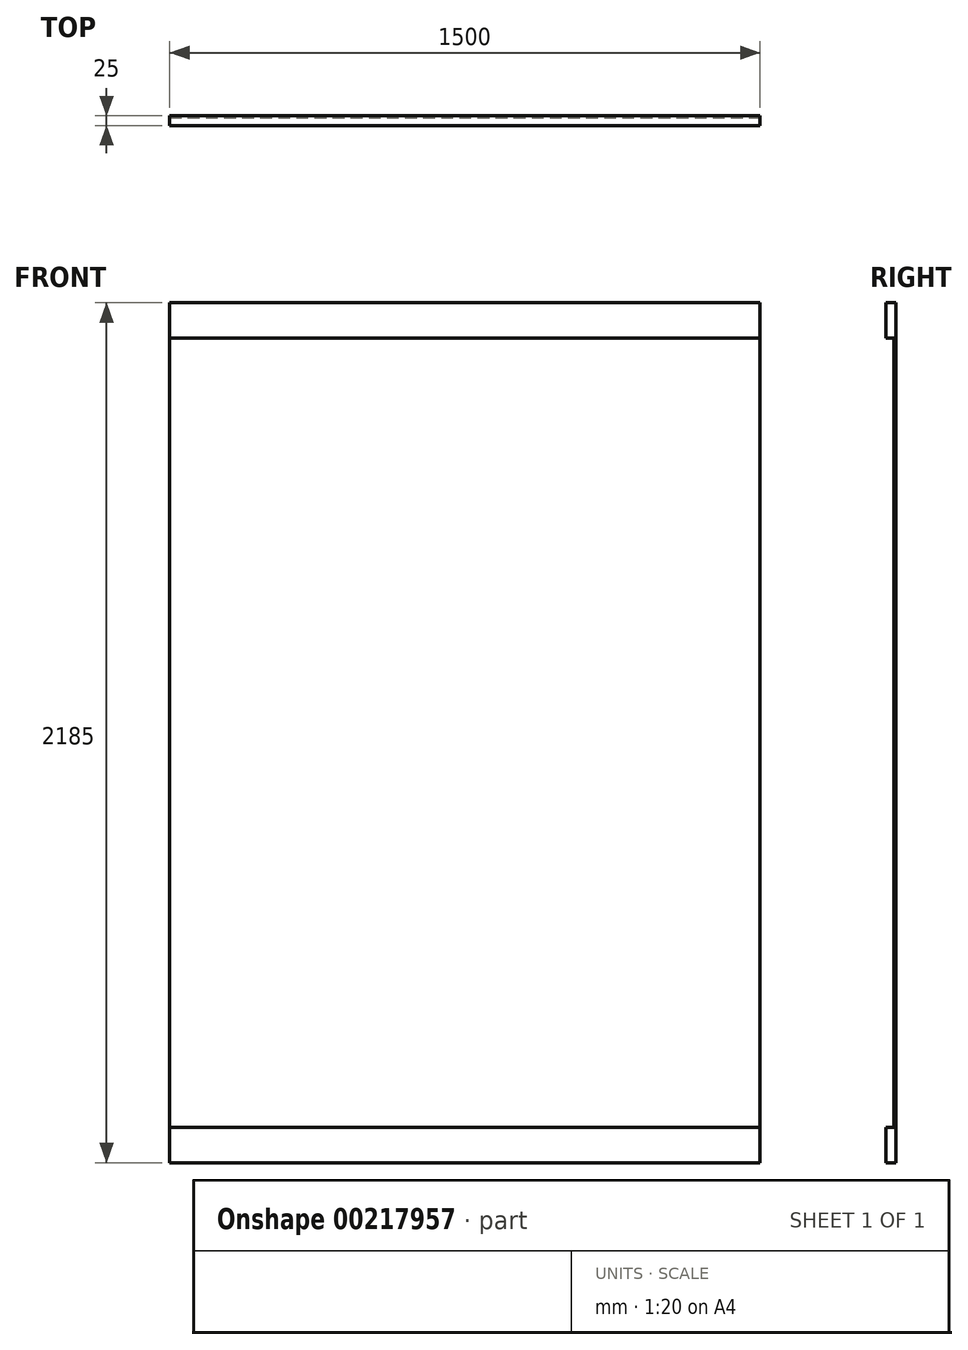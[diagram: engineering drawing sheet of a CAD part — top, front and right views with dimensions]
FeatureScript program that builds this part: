
annotation { "Feature Type Name" : "Feature", "Feature Type Description" : "" }
export const myFeature = defineFeature(function(context is Context, id is Id, definition is map)
    precondition{}
    {
        {
            var Q0;
            Q0=qCreatedBy(makeId("Front.planeOp"),FACE);
            var sketch = newSketch(context, id + "F0", { "sketchPlane" : qUnion([Q0])});
            skLineSegment(sketch, "E0.bottom", {"start": v(0, 0) * mm, "end": v(1500, 0) * mm});
            skLineSegment(sketch, "E0.top", {"start": v(0, -2005) * mm, "end": v(1500, -2005) * mm});
            skLineSegment(sketch, "E0.left", {"start": v(0, 0) * mm, "end": v(0, -2005) * mm});
            skLineSegment(sketch, "E0.right", {"start": v(1500, 0) * mm, "end": v(1500, -2005) * mm});
            skLineSegment(sketch, "E1.bottom", {"start": v(0, 0) * mm, "end": v(1500, 0) * mm, "construction": true});
            skLineSegment(sketch, "E1.top", {"start": v(0, 90) * mm, "end": v(1500, 90) * mm});
            skLineSegment(sketch, "E1.left", {"start": v(0, 0) * mm, "end": v(0, 90) * mm});
            skLineSegment(sketch, "E1.right", {"start": v(1500, 0) * mm, "end": v(1500, 90) * mm});
            skLineSegment(sketch, "E2.bottom", {"start": v(0, -2005) * mm, "end": v(1500, -2005) * mm, "construction": true});
            skLineSegment(sketch, "E2.top", {"start": v(0, -2095) * mm, "end": v(1500, -2095) * mm});
            skLineSegment(sketch, "E2.left", {"start": v(0, -2005) * mm, "end": v(0, -2095) * mm});
            skLineSegment(sketch, "E2.right", {"start": v(1500, -2005) * mm, "end": v(1500, -2095) * mm});
            skSolve(sketch);
        }
        {
            var Q0;
            Q0=makeQuery(id+"F0.imprint","IMPRINT",FACE,{"disambiguationData":[TD([[makeQuery(id+"F0.imprint","IMPRINT",EDGE,{"derivedFrom":sQuery(id+"F0.wireOp",EDGE,"E0.bottom")}),1.0]])]});
            var Q1;
            Q1=makeQuery(id+"F0.imprint","IMPRINT",FACE,{"disambiguationData":[TD([[makeQuery(id+"F0.imprint","IMPRINT",EDGE,{"derivedFrom":sQuery(id+"F0.wireOp",EDGE,"E0.top")}),-1.0]])]});
            extrude(context, id + "F1", {"entities" : qUnion([Q0, Q1]), "depth" : 25 * mm});
        }
        {
            var Q0;
            Q0=makeQuery(id+"F0.imprint","IMPRINT",FACE,{"disambiguationData":[TD([[makeQuery(id+"F0.imprint","IMPRINT",EDGE,{"derivedFrom":sQuery(id+"F0.wireOp",EDGE,"E0.bottom")}),-1.0]])]});
            extrude(context, id + "F2", {"entities" : qUnion([Q0]), "depth" : 5 * mm});
        }
    });
